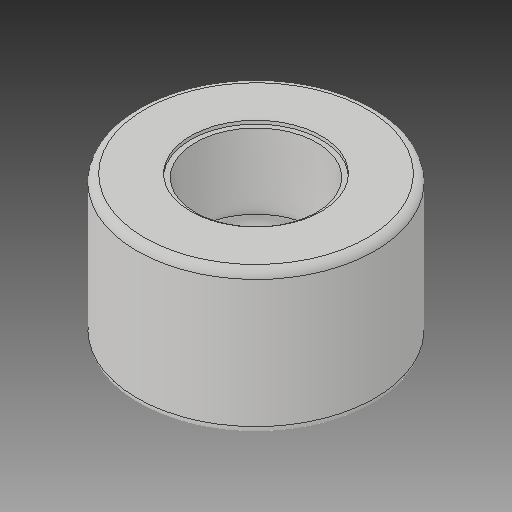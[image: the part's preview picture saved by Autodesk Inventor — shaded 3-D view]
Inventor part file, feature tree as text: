
AUTODESK INVENTOR PART (.ipt)
format: ipt  version: 2019 (Build 230136000, 136)  size: 181,248 bytes
history: native  units: in
note: dims shown in document units (in); Inventor stores cm internally (conversion verified against a paired STEP export)
features: fillet x1
ambient origin geometry x8: Origin, YZ Plane, XZ Plane, XY Plane, X Axis, Y Axis, Z Axis, Center Point
bodies: Solid1 (feature_tree)
feature tree (1):
  fillet  "Fillet1"  [1 undecoded]
note: 1 required parameter value undecoded (feature->parameter linkage not recoverable at this tier; creation-order binding heuristic only, values carry confidence <= 0.55)
